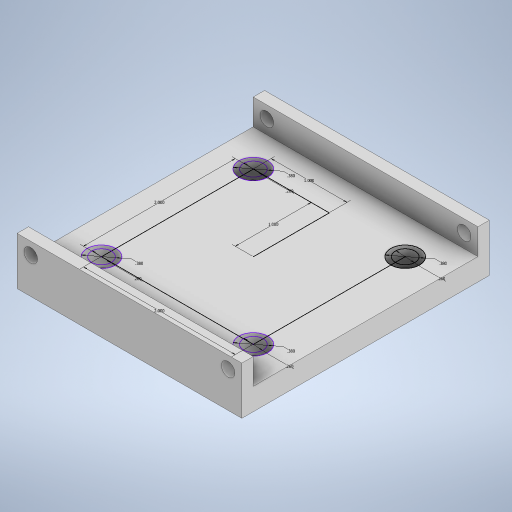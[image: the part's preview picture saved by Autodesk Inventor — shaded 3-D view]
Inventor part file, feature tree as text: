
AUTODESK INVENTOR PART (.ipt)
format: ipt  version: 2024.2 (Build 282272000, 272)  size: 311,808 bytes
history: native  units: in
note: dims shown in document units (in); Inventor stores cm internally (conversion verified against a paired STEP export)
features: sketch x6, extrude x5
ambient origin geometry x8: Origin, YZ Plane, XZ Plane, XY Plane, X Axis, Y Axis, Z Axis, Center Point
bodies: Solid1 (feature_tree)
feature tree (11):
  extrude  "Extrusion1"  Depth=2.96in
  sketch  "Sketch6"  dims[d11=0.26in d12=0.38in d13=0.26in d14=0.38in d15=0.26in d16=0.38in d21=0.15in d22=0.15in d23=0.63in d24=0.0in d25=0.18in d26=0.18in d27=0.18in d35=1.0in d36=1.0in d37=2.0in d38=2.0in d39=0.26in d40=0.38in d41=0.26in d42=0.38in d43=0.26in d44=0.38in d45=0.26in d46=0.38in d47=1.0in d48=0.0in d49=0.26in d50=0.0in d51=0.18in d52=0.18in d53=5.0in d54=0.0in]
  sketch  "Sketch2"  dims[d2=0.29in d3=0.0in d4=0.5in]
  sketch  "Sketch3"  dims[d5=0.5in d6=1.0in]
  extrude  "Extrusion4"  Depth=0.29in
  sketch  "Sketch5"  dims[d9=0.26in d10=0.38in]
  extrude  "Extrusion5"  Depth=1.0in
  extrude  "Extrusion6"  Depth=1.0in
  extrude  "Extrusion7"  Depth=0.26in
  sketch  "Sketch1"  dims[d0=2.96in d1=2.96in]
  sketch  "Sketch4"  dims[d7=1.0in d8=1.0in]
